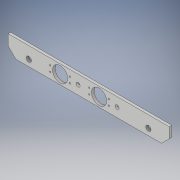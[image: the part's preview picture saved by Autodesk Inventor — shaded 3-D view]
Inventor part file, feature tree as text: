
AUTODESK INVENTOR PART (.ipt)
format: ipt  version: 2017 (Build 210142000, 142)  size: 144,896 bytes
history: native  units: in
note: dims shown in document units (in); Inventor stores cm internally (conversion verified against a paired STEP export)
features: chamfer x3, extrude x2, sketch x1
ambient origin geometry x8: Origin, YZ Plane, XZ Plane, XY Plane, X Axis, Y Axis, Z Axis, Center Point
bodies: Solid1 (feature_tree)
feature tree (6):
  sketch  "Sketch1"  dims[d3=1.46in d5=1.46in d10=0.14in d11=0.14in d24=0.276in d28=0.138in d29=0.138in d30=0.138in d31=0.945in d38=0.138in d39=0.138in d40=0.138in d41=0.138in d48=0.25in d49=0.0in d50=0.125in d51=0.125in d52=45.0deg d56=1.0in d57=0.0in d58=0.75in d59=0.125in d60=45.0deg d61=0.75in d62=0.125in d63=45.0deg d12=1.0in d13=1.0in]
  extrude  "Extrusion4"  Depth=0.125in
  chamfer  "Chamfer2"  Distance=0.14in
  extrude  "Extrusion5"  Depth=0.125in
  chamfer  "Chamfer3"  Distance=0.276in
  chamfer  "Chamfer4"  Distance=0.138in
